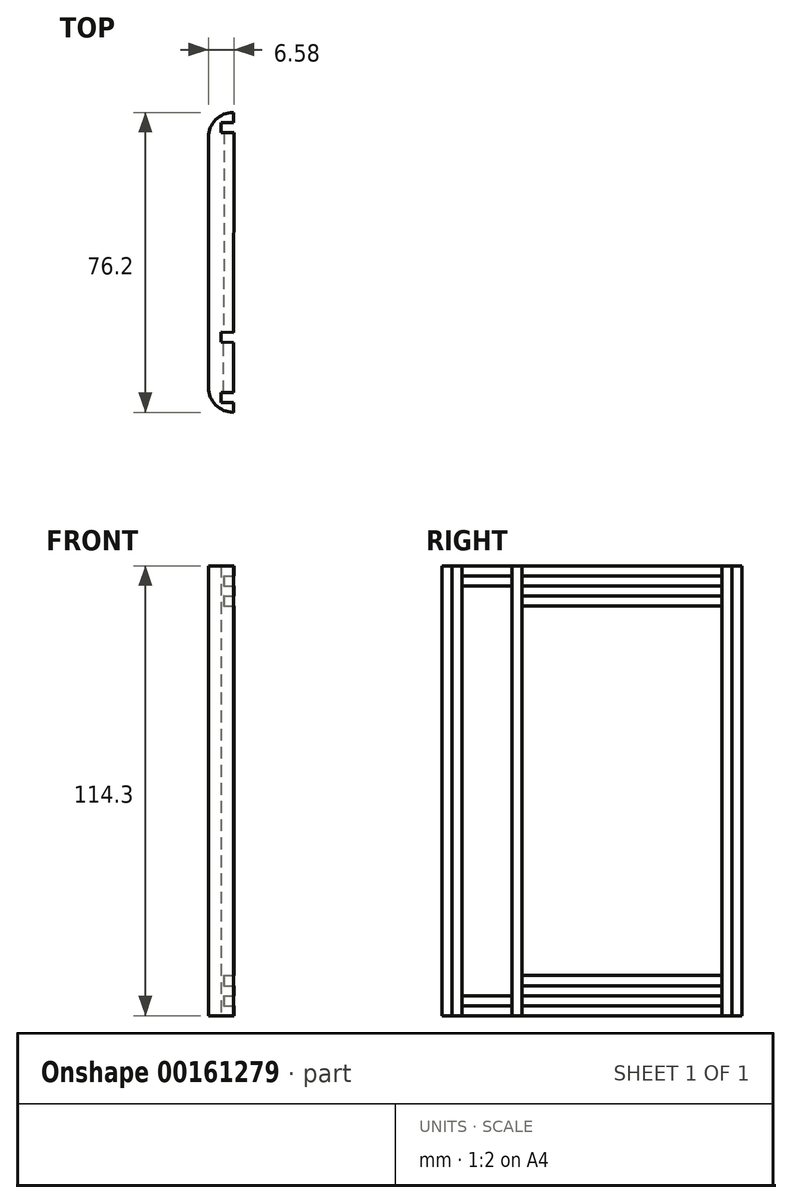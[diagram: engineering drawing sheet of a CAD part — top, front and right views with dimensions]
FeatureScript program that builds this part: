
annotation { "Feature Type Name" : "Feature", "Feature Type Description" : "" }
export const myFeature = defineFeature(function(context is Context, id is Id, definition is map)
    precondition{}
    {
        {
            var Q0;
            Q0=qCreatedBy(makeId("Top.planeOp"),FACE);
            var sketch = newSketch(context, id + "F0", { "sketchPlane" : qUnion([Q0])});
            skLineSegment(sketch, "E0.right", {"start": v(-3.17, 38.1) * mm, "end": v(-3.18, -38.1) * mm});
            skPoint(sketch, "E0.middle", {"position": v(0, 0) * mm});
            skLineSegment(sketch, "E1.trimOffspring", {"start": v(3.4, 33.02) * mm, "end": v(3.24, -17.78) * mm});
            skLineSegment(sketch, "E2", {"start": v(-3.17, 38.1) * mm, "end": v(3.18, 38.1) * mm});
            skLineSegment(sketch, "E3", {"start": v(3.18, 35.56) * mm, "end": v(0, 35.56) * mm});
            skLineSegment(sketch, "E4", {"start": v(3.18, 35.56) * mm, "end": v(3.18, 38.1) * mm});
            skLineSegment(sketch, "E5", {"start": v(0, 35.56) * mm, "end": v(0, 33.02) * mm});
            skLineSegment(sketch, "E6", {"start": v(3.4, 33.02) * mm, "end": v(0, 33.02) * mm});
            skLineSegment(sketch, "E7", {"start": v(-3.18, -38.1) * mm, "end": v(3.18, -38.1) * mm});
            skLineSegment(sketch, "E8", {"start": v(0, -35.56) * mm, "end": v(0, -33.02) * mm});
            skLineSegment(sketch, "E9", {"start": v(0, -20.3) * mm, "end": v(0, -17.77) * mm});
            skLineSegment(sketch, "E10", {"start": v(0, -35.56) * mm, "end": v(3.18, -35.56) * mm});
            skLineSegment(sketch, "E11", {"start": v(3.2, -33.02) * mm, "end": v(3.2, -33.02) * mm});
            skLineSegment(sketch, "E12", {"start": v(0, -20.3) * mm, "end": v(3.23, -20.32) * mm});
            skLineSegment(sketch, "E13", {"start": v(0, -17.77) * mm, "end": v(3.24, -17.78) * mm});
            skLineSegment(sketch, "E14.trimOffspring", {"start": v(3.23, -20.32) * mm, "end": v(3.2, -33.02) * mm});
            skLineSegment(sketch, "E15.trimOffspring", {"start": v(3.18, -35.56) * mm, "end": v(3.18, -38.1) * mm});
            skLineSegment(sketch, "E16", {"start": v(0, -33.02) * mm, "end": v(3.2, -33.02) * mm});
            skSolve(sketch);
        }
        {
            var Q0;
            Q0=makeQuery(id+"F0.imprint","IMPRINT",FACE,{"disambiguationData":[TD([[makeQuery(id+"F0.imprint","IMPRINT",EDGE,{"derivedFrom":sQuery(id+"F0.wireOp",EDGE,"E0.right")}),1.0]])]});
            extrude(context, id + "F1", {"entities" : qUnion([Q0]), "depth" : 114.3 * mm});
        }
        {
            var Q0;
            Q0=makeQuery(id+"F1.opExtrude","SWEPT_EDGE",EDGE,{"disambiguationData":[OSD([sQuery(id+"F0.wireOp",EDGE,"E0.bottom"),sQuery(id+"F0.wireOp",EDGE,"E0.right")])]});
            fillet(context, id + "F2", {"entities" : qUnion([Q0]), "radius" : 6.35 * mm, "tangentPropagation" : true, "allowEdgeOverflow" : false});
        }
        {
            var Q0;
            Q0=makeQuery(id+"F1.opExtrude","SWEPT_FACE",FACE,{"disambiguationData":[OSD([sQuery(id+"F0.wireOp",EDGE,"E1.trimOffspring")])]});
            var sketch = newSketch(context, id + "F3", { "sketchPlane" : qUnion([Q0])});
            skLineSegment(sketch, "E17.bottom", {"start": v(-17.77, 111.76) * mm, "end": v(33.03, 111.76) * mm});
            skLineSegment(sketch, "E17.top", {"start": v(-17.77, 109.22) * mm, "end": v(33.03, 109.22) * mm});
            skLineSegment(sketch, "E17.left", {"start": v(-17.77, 111.76) * mm, "end": v(-17.77, 109.22) * mm});
            skLineSegment(sketch, "E17.right", {"start": v(33.03, 111.76) * mm, "end": v(33.03, 109.22) * mm});
            skLineSegment(sketch, "E18.bottom", {"start": v(-17.77, 2.54) * mm, "end": v(33.03, 2.54) * mm});
            skLineSegment(sketch, "E18.top", {"start": v(-17.77, 5.08) * mm, "end": v(33.03, 5.08) * mm});
            skLineSegment(sketch, "E18.left", {"start": v(-17.77, 2.54) * mm, "end": v(-17.77, 5.08) * mm});
            skLineSegment(sketch, "E18.right", {"start": v(33.03, 2.54) * mm, "end": v(33.03, 5.08) * mm});
            skLineSegment(sketch, "E19", {"start": v(33.03, 109.22) * mm, "end": v(33.03, 106.68) * mm});
            skLineSegment(sketch, "E20", {"start": v(33.03, 106.68) * mm, "end": v(-17.77, 106.68) * mm});
            skLineSegment(sketch, "E21", {"start": v(-17.77, 106.68) * mm, "end": v(-17.77, 104.14) * mm});
            skLineSegment(sketch, "E22", {"start": v(-17.77, 104.14) * mm, "end": v(33.03, 104.14) * mm});
            skLineSegment(sketch, "E23", {"start": v(33.03, 104.14) * mm, "end": v(33.03, 106.68) * mm});
            skLineSegment(sketch, "E24", {"start": v(33.03, 5.08) * mm, "end": v(33.03, 7.63) * mm});
            skLineSegment(sketch, "E25", {"start": v(33.03, 7.63) * mm, "end": v(-17.77, 7.63) * mm});
            skLineSegment(sketch, "E26", {"start": v(-17.77, 7.63) * mm, "end": v(-17.77, 10.18) * mm});
            skLineSegment(sketch, "E27", {"start": v(-17.77, 10.18) * mm, "end": v(33.03, 10.18) * mm});
            skLineSegment(sketch, "E28", {"start": v(33.03, 10.18) * mm, "end": v(33.03, 7.63) * mm});
            skSolve(sketch);
        }
        {
            var Q0;
            Q0=makeQuery(id+"F3.imprint","IMPRINT",FACE,{"disambiguationData":[TD([[makeQuery(id+"F3.imprint","IMPRINT",EDGE,{"derivedFrom":sQuery(id+"F3.wireOp",EDGE,"E17.bottom")}),-1.0]])]});
            var Q1;
            Q1=makeQuery(id+"F3.imprint","IMPRINT",FACE,{"disambiguationData":[TD([[makeQuery(id+"F3.imprint","IMPRINT",EDGE,{"derivedFrom":sQuery(id+"F3.wireOp",EDGE,"E20")}),1.0]])]});
            var Q2;
            Q2=makeQuery(id+"F3.imprint","IMPRINT",FACE,{"disambiguationData":[TD([[makeQuery(id+"F3.imprint","IMPRINT",EDGE,{"derivedFrom":sQuery(id+"F3.wireOp",EDGE,"E18.bottom")}),1.0]])]});
            var Q3;
            Q3=makeQuery(id+"F3.imprint","IMPRINT",FACE,{"disambiguationData":[TD([[makeQuery(id+"F3.imprint","IMPRINT",EDGE,{"derivedFrom":sQuery(id+"F3.wireOp",EDGE,"E25")}),-1.0]])]});
            extrude(context, id + "F4", {"entities" : qUnion([Q0, Q1, Q2, Q3]), "operationType" : NewBodyOperationType.REMOVE, "oppositeDirection" : true, "depth" : 2.54 * mm});
        }
        {
            var Q0;
            Q0=makeQuery(id+"F1.opExtrude","SWEPT_FACE",FACE,{"disambiguationData":[OSD([sQuery(id+"F0.wireOp",EDGE,"E14.trimOffspring")])]});
            var sketch = newSketch(context, id + "F5", { "sketchPlane" : qUnion([Q0])});
            skLineSegment(sketch, "E29.bottom", {"start": v(-33, 111.76) * mm, "end": v(-20.3, 111.76) * mm});
            skLineSegment(sketch, "E29.top", {"start": v(-33, 109.22) * mm, "end": v(-20.3, 109.22) * mm});
            skLineSegment(sketch, "E29.left", {"start": v(-33, 111.76) * mm, "end": v(-33, 109.22) * mm});
            skLineSegment(sketch, "E29.right", {"start": v(-20.3, 111.76) * mm, "end": v(-20.3, 109.22) * mm});
            skLineSegment(sketch, "E30.bottom", {"start": v(-33, 2.54) * mm, "end": v(-20.3, 2.54) * mm});
            skLineSegment(sketch, "E30.top", {"start": v(-33, 5.08) * mm, "end": v(-20.3, 5.08) * mm});
            skLineSegment(sketch, "E30.left", {"start": v(-33, 2.54) * mm, "end": v(-33, 5.08) * mm});
            skLineSegment(sketch, "E30.right", {"start": v(-20.3, 2.54) * mm, "end": v(-20.3, 5.08) * mm});
            skSolve(sketch);
        }
        {
            var Q0;
            Q0=makeQuery(id+"F5.imprint","IMPRINT",FACE,{"disambiguationData":[TD([[makeQuery(id+"F5.imprint","IMPRINT",EDGE,{"derivedFrom":sQuery(id+"F5.wireOp",EDGE,"E30.bottom")}),1.0]])]});
            var Q1;
            Q1=makeQuery(id+"F5.imprint","IMPRINT",FACE,{"disambiguationData":[TD([[makeQuery(id+"F5.imprint","IMPRINT",EDGE,{"derivedFrom":sQuery(id+"F5.wireOp",EDGE,"E29.bottom")}),-1.0]])]});
            extrude(context, id + "F6", {"entities" : qUnion([Q0, Q1]), "operationType" : NewBodyOperationType.REMOVE, "oppositeDirection" : true, "depth" : 2.54 * mm});
        }
    });
